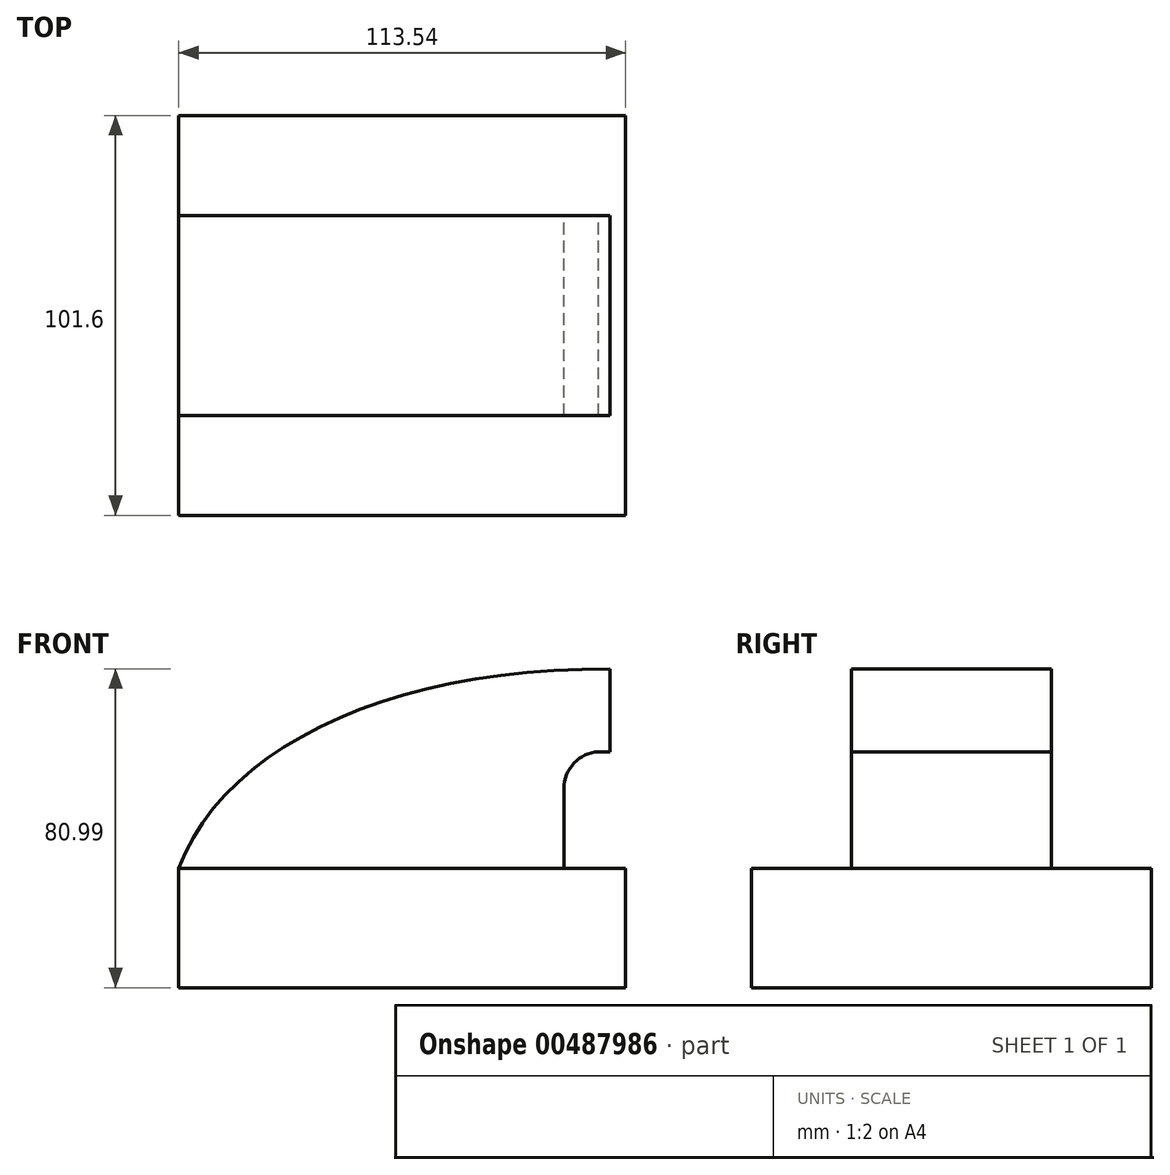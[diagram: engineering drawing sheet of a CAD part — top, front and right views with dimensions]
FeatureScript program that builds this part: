
annotation { "Feature Type Name" : "Feature", "Feature Type Description" : "" }
export const myFeature = defineFeature(function(context is Context, id is Id, definition is map)
    precondition{}
    {
        {
            var Q0;
            Q0=qCreatedBy(makeId("Front.planeOp"),FACE);
            var sketch = newSketch(context, id + "F0", { "sketchPlane" : qUnion([Q0])});
            skLineSegment(sketch, "E0.bottom", {"start": v(-56.77, -15.17) * mm, "end": v(56.77, -15.17) * mm});
            skLineSegment(sketch, "E0.top", {"start": v(-56.77, 15.17) * mm, "end": v(56.77, 15.17) * mm});
            skLineSegment(sketch, "E0.left", {"start": v(-56.77, -15.17) * mm, "end": v(-56.77, 15.17) * mm});
            skLineSegment(sketch, "E0.right", {"start": v(56.77, -15.17) * mm, "end": v(56.77, 15.17) * mm});
            skPoint(sketch, "E0.middle", {"position": v(0, 0) * mm});
            skLineSegment(sketch, "E1.bottom", {"start": v(97.87, 41.35) * mm, "end": v(52.85, 41.35) * mm});
            skLineSegment(sketch, "E1.top", {"start": v(97.87, 65.82) * mm, "end": v(52.85, 65.82) * mm});
            skLineSegment(sketch, "E1.left", {"start": v(97.87, 41.35) * mm, "end": v(97.87, 65.82) * mm});
            skLineSegment(sketch, "E1.right", {"start": v(52.85, 41.35) * mm, "end": v(52.85, 65.82) * mm});
            skPoint(sketch, "E1.middle", {"position": v(75.36, 53.58) * mm});
            skLineSegment(sketch, "E2", {"start": v(41.1, 15.17) * mm, "end": v(41.1, 35.48) * mm});
            skFitSpline(sketch, "E3", {"points": [v(-56.77, 15.17) * mm, v(52.85, 65.82) * mm], "startDerivative": vector(35.23, 93.22) * mm, "endDerivative": vector(167.36, -0.73) * mm});
            skArc(sketch, "E4", {"start": v(41.1, 35.48) * mm, "mid": v(43.66, 41.88) * mm, "end": v(49.91, 44.78) * mm});
            skLineSegment(sketch, "E5", {"start": v(49.91, 44.78) * mm, "end": v(75.36, 44.78) * mm});
            skLineSegment(sketch, "E6", {"start": v(75.36, 53.58) * mm, "end": v(75.36, 41.35) * mm});
            skLineSegment(sketch, "E7", {"start": v(75.36, 53.58) * mm, "end": v(75.36, 65.82) * mm});
            skSolve(sketch);
        }
        {
            var Q0;
            Q0=makeQuery(id+"F0.imprint","IMPRINT",FACE,{"disambiguationData":[TD([[makeQuery(id+"F0.imprint","IMPRINT",EDGE,{"derivedFrom":sQuery(id+"F0.wireOp",EDGE,"E0.bottom")}),1.0]])]});
            extrude(context, id + "F1", {"entities" : qUnion([Q0]), "depth" : 50.8 * mm, "hasSecondDirection" : true, "secondDirectionOppositeDirection" : true, "secondDirectionDepth" : 50.8 * mm});
        }
        {
            var Q0;
            {var subQ1=sQuery(id+"F0.wireOp",EDGE,"E2");Q0=makeQuery(id+"F0.imprint","IMPRINT",FACE,{"disambiguationData":[TD([[makeQuery(id+"F0.imprint","IMPRINT",EDGE,{"derivedFrom":subQ1}),1.0]])]});}
            extrude(context, id + "F2", {"entities" : qUnion([Q0]), "operationType" : NewBodyOperationType.ADD, "depth" : 25.4 * mm, "hasSecondDirection" : true, "secondDirectionOppositeDirection" : true, "secondDirectionDepth" : 25.4 * mm});
        }
    });
